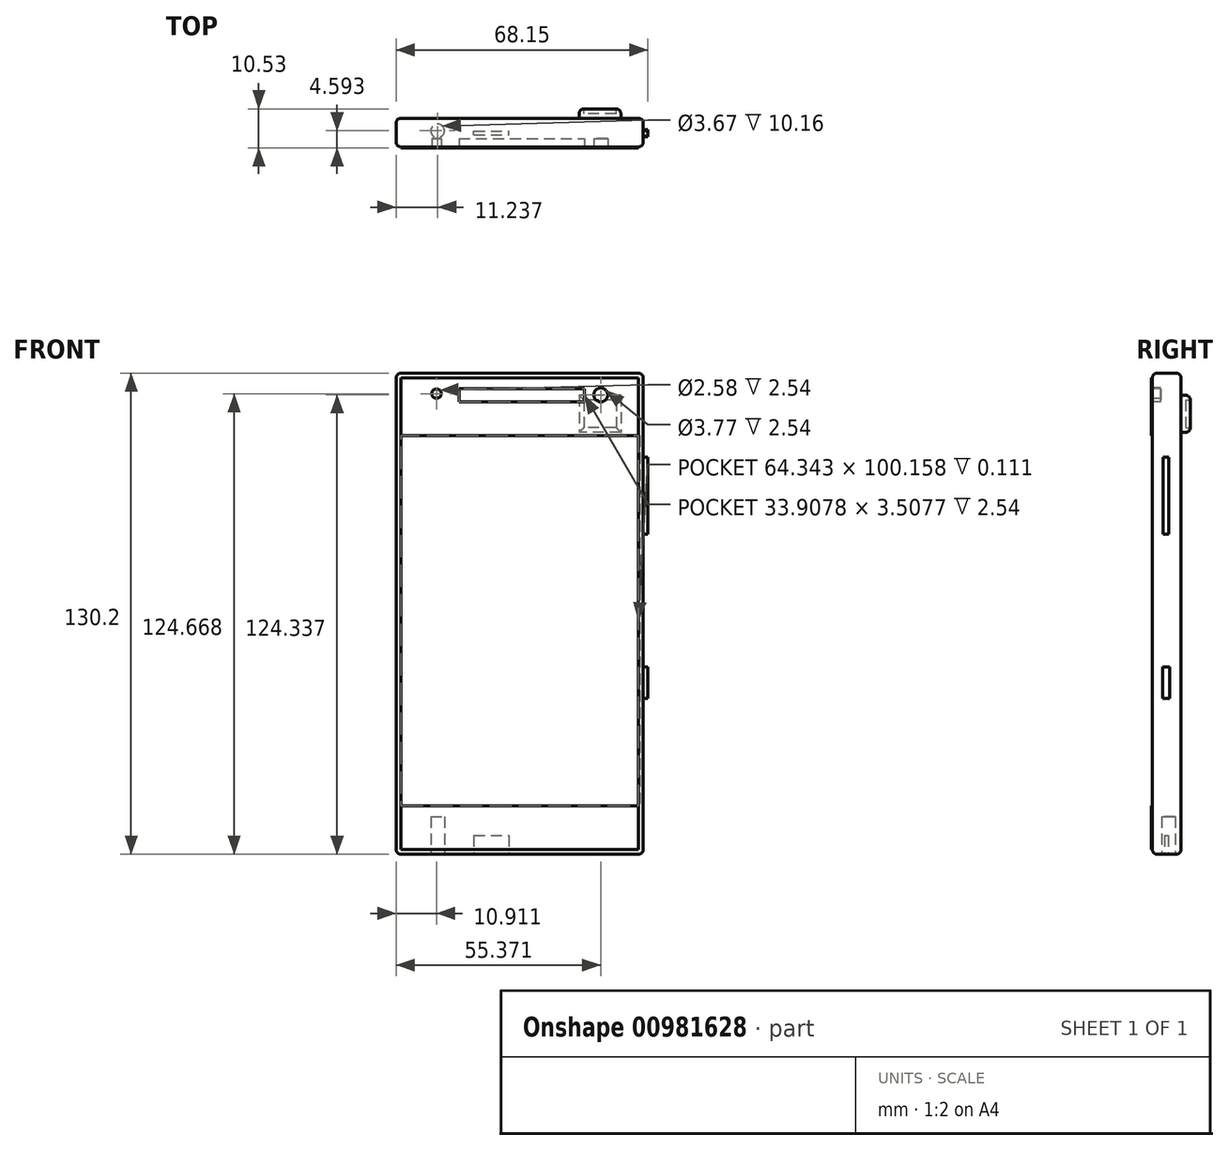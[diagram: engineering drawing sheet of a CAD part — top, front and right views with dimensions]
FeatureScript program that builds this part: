
annotation { "Feature Type Name" : "Feature", "Feature Type Description" : "" }
export const myFeature = defineFeature(function(context is Context, id is Id, definition is map)
    precondition{}
    {
        {
            var Q0;
            Q0=qCreatedBy(makeId("Front.planeOp"),FACE);
            var sketch = newSketch(context, id + "F0", { "sketchPlane" : qUnion([Q0])});
            skLineSegment(sketch, "E0.bottom", {"start": v(33.44, -65.1) * mm, "end": v(-33.44, -65.1) * mm});
            skLineSegment(sketch, "E0.top", {"start": v(33.44, 65.1) * mm, "end": v(-33.44, 65.1) * mm});
            skLineSegment(sketch, "E0.left", {"start": v(33.44, -65.1) * mm, "end": v(33.44, 65.1) * mm});
            skLineSegment(sketch, "E0.right", {"start": v(-33.44, -65.1) * mm, "end": v(-33.44, 65.1) * mm});
            skPoint(sketch, "E0.middle", {"position": v(0, 0) * mm});
            skSolve(sketch);
        }
        {
            var Q0;
            Q0 = qSketchRegion(id + "F0", true);
            extrude(context, id + "F1", {"entities" : qUnion([Q0]), "depth" : 7.73 * mm, "offsetDistance" : 25.4 * mm});
        }
        {
            var Q0;
            Q0=makeQuery(id+"F1.opExtrude","CAP_FACE",FACE,{"disambiguationData":[OSD([sQuery(id+"F0.wireOp",EDGE,"E0.bottom"),sQuery(id+"F0.wireOp",EDGE,"E0.top"),sQuery(id+"F0.wireOp",EDGE,"E0.left"),sQuery(id+"F0.wireOp",EDGE,"E0.right")])],"isStart":false});
            var Q1;
            Q1=makeQuery(id+"F1.opExtrude","CAP_FACE",FACE,{"disambiguationData":[OSD([sQuery(id+"F0.wireOp",EDGE,"E0.bottom"),sQuery(id+"F0.wireOp",EDGE,"E0.top"),sQuery(id+"F0.wireOp",EDGE,"E0.left"),sQuery(id+"F0.wireOp",EDGE,"E0.right")])],"isStart":true});
            var Q2;
            Q2=makeQuery(id+"F1.opExtrude","SWEPT_EDGE",EDGE,{"disambiguationData":[OSD([sQuery(id+"F0.wireOp",EDGE,"E0.top"),sQuery(id+"F0.wireOp",EDGE,"E0.right")])]});
            var Q3;
            Q3=makeQuery(id+"F1.opExtrude","SWEPT_EDGE",EDGE,{"disambiguationData":[OSD([sQuery(id+"F0.wireOp",EDGE,"E0.bottom"),sQuery(id+"F0.wireOp",EDGE,"E0.left")])]});
            var Q4;
            Q4=makeQuery(id+"F1.opExtrude","SWEPT_EDGE",EDGE,{"disambiguationData":[OSD([sQuery(id+"F0.wireOp",EDGE,"E0.top"),sQuery(id+"F0.wireOp",EDGE,"E0.left")])]});
            var Q5;
            Q5=makeQuery(id+"F1.opExtrude","SWEPT_EDGE",EDGE,{"disambiguationData":[OSD([sQuery(id+"F0.wireOp",EDGE,"E0.bottom"),sQuery(id+"F0.wireOp",EDGE,"E0.right")])]});
            fillet(context, id + "F2", {"entities" : qUnion([Q0, Q1, Q2, Q3, Q4, Q5]), "radius" : 1.27 * mm, "tangentPropagation" : true, "allowEdgeOverflow" : false});
        }
        {
            var Q0;
            Q0=qCreatedBy(makeId("Front.planeOp"),FACE);
            var sketch = newSketch(context, id + "F3", { "sketchPlane" : qUnion([Q0])});
            skLineSegment(sketch, "E1.bottom", {"start": v(-32.55, -50.39) * mm, "end": v(32.55, -50.39) * mm});
            skLineSegment(sketch, "E1.top", {"start": v(-32.55, 50.39) * mm, "end": v(32.55, 50.39) * mm});
            skLineSegment(sketch, "E1.left", {"start": v(-32.55, -50.39) * mm, "end": v(-32.55, 50.39) * mm});
            skLineSegment(sketch, "E1.right", {"start": v(32.55, -50.39) * mm, "end": v(32.55, 50.39) * mm});
            skSolve(sketch);
        }
        {
            var Q0;
            Q0 = qSketchRegion(id + "F3", true);
            var Q1;
            Q1=makeQuery(id+"F1.opExtrude","CAP_FACE",FACE,{"disambiguationData":[OSD([sQuery(id+"F0.wireOp",EDGE,"E0.bottom"),sQuery(id+"F0.wireOp",EDGE,"E0.top"),sQuery(id+"F0.wireOp",EDGE,"E0.left"),sQuery(id+"F0.wireOp",EDGE,"E0.right")])],"isStart":false});
            extrude(context, id + "F4", {"entities" : qUnion([Q0, Q1]), "operationType" : NewBodyOperationType.REMOVE, "oppositeDirection" : true, "depth" : 2.3 * mm, "offsetDistance" : 25.4 * mm});
        }
        {
            var Q0;
            Q0=qCreatedBy(makeId("Front.planeOp"),FACE);
            var sketch = newSketch(context, id + "F5", { "sketchPlane" : qUnion([Q0])});
            skLineSegment(sketch, "E2.bottom", {"start": v(-32.44, 48.2) * mm, "end": v(32.5, 48.2) * mm});
            skLineSegment(sketch, "E2.top", {"start": v(-32.44, -51.95) * mm, "end": v(32.5, -51.95) * mm});
            skLineSegment(sketch, "E2.left", {"start": v(-32.44, 48.2) * mm, "end": v(-32.44, -51.95) * mm});
            skLineSegment(sketch, "E2.right", {"start": v(32.5, 48.2) * mm, "end": v(32.5, -51.95) * mm});
            skSolve(sketch);
        }
        {
            var Q0;
            Q0 = qSketchRegion(id + "F5", true);
            extrude(context, id + "F6", {"entities" : qUnion([Q0]), "operationType" : NewBodyOperationType.ADD, "depth" : 7.62 * mm, "offsetDistance" : 25.4 * mm});
        }
        {
            var Q0;
            {var subQ0=sQuery(id+"F0.wireOp",EDGE,"E0.right");var subQ1=sQuery(id+"F0.wireOp",EDGE,"E0.left");var subQ2=sQuery(id+"F0.wireOp",EDGE,"E0.top");var subQ3=sQuery(id+"F0.wireOp",EDGE,"E0.bottom");Q0=makeQuery(id+"F6.boolean.opBoolean","SPLIT",FACE,{"disambiguationData":[TD([makeQuery(id+"F6.opExtrude","SWEPT_FACE",FACE,{"disambiguationData":[OSD([sQuery(id+"F5.wireOp",EDGE,"E2.bottom")])]})])],"derivedFrom":makeQuery(id+"F4.boolean.opBoolean","COPY",FACE,{"derivedFrom":makeQuery(id+"F4.opExtrude","CAP_FACE",FACE,{"disambiguationData":[OSD([subQ3,subQ2,subQ1,subQ0])],"isStart":false})})});}
            var sketch = newSketch(context, id + "F7", { "sketchPlane" : qUnion([Q0])});
            skLineSegment(sketch, "E3.bottom", {"start": v(-32.17, 48.2) * mm, "end": v(32.17, 48.2) * mm});
            skLineSegment(sketch, "E3.top", {"start": v(-32.17, 63.83) * mm, "end": v(32.17, 63.83) * mm});
            skLineSegment(sketch, "E3.left", {"start": v(-32.17, 48.2) * mm, "end": v(-32.17, 63.83) * mm});
            skLineSegment(sketch, "E3.right", {"start": v(32.17, 48.2) * mm, "end": v(32.17, 63.83) * mm});
            skSolve(sketch);
        }
        {
            var Q0;
            Q0 = qSketchRegion(id + "F7", true);
            extrude(context, id + "F8", {"entities" : qUnion([Q0]), "operationType" : NewBodyOperationType.ADD, "depth" : 2.54 * mm, "offsetDistance" : 25.4 * mm});
        }
        {
            var Q0;
            Q0=makeQuery(id+"F8.opExtrude","CAP_FACE",FACE,{"disambiguationData":[OSD([sQuery(id+"F7.wireOp",EDGE,"E3.bottom"),sQuery(id+"F7.wireOp",EDGE,"E3.top"),sQuery(id+"F7.wireOp",EDGE,"E3.left"),sQuery(id+"F7.wireOp",EDGE,"E3.right")])],"isStart":false});
            var sketch = newSketch(context, id + "F9", { "sketchPlane" : qUnion([Q0])});
            skLineSegment(sketch, "E4.bottom", {"start": v(-16.45, 60.86) * mm, "end": v(17.46, 60.86) * mm});
            skLineSegment(sketch, "E4.top", {"start": v(-16.45, 57.35) * mm, "end": v(17.46, 57.35) * mm});
            skLineSegment(sketch, "E4.left", {"start": v(-16.45, 60.86) * mm, "end": v(-16.45, 57.35) * mm});
            skLineSegment(sketch, "E4.right", {"start": v(17.46, 60.86) * mm, "end": v(17.46, 57.35) * mm});
            skCircle(sketch, "E5", {"center": v(-22.53, 59.57) * mm, "radius": 1.29 * mm});
            skCircle(sketch, "E6", {"center": v(21.93, 59.24) * mm, "radius": 1.89 * mm});
            skSolve(sketch);
        }
        {
            var Q0;
            Q0 = qSketchRegion(id + "F9", true);
            extrude(context, id + "F10", {"entities" : qUnion([Q0]), "operationType" : NewBodyOperationType.REMOVE, "oppositeDirection" : true, "depth" : 2.54 * mm, "offsetDistance" : 25.4 * mm});
        }
        {
            var Q0;
            Q0 = qSketchRegion(id + "F9", true);
            extrude(context, id + "F11", {"entities" : qUnion([Q0]), "operationType" : NewBodyOperationType.REMOVE, "oppositeDirection" : true, "depth" : 2.54 * mm, "offsetDistance" : 25.4 * mm});
        }
        {
            var Q0;
            {var subQ0=sQuery(id+"F0.wireOp",EDGE,"E0.right");var subQ1=sQuery(id+"F0.wireOp",EDGE,"E0.left");var subQ2=sQuery(id+"F0.wireOp",EDGE,"E0.top");var subQ3=sQuery(id+"F0.wireOp",EDGE,"E0.bottom");Q0=makeQuery(id+"F6.boolean.opBoolean","SPLIT",FACE,{"disambiguationData":[TD([makeQuery(id+"F6.opExtrude","SWEPT_FACE",FACE,{"disambiguationData":[OSD([sQuery(id+"F5.wireOp",EDGE,"E2.top")])]})])],"derivedFrom":makeQuery(id+"F4.boolean.opBoolean","COPY",FACE,{"derivedFrom":makeQuery(id+"F4.opExtrude","CAP_FACE",FACE,{"disambiguationData":[OSD([subQ3,subQ2,subQ1,subQ0])],"isStart":false})})});}
            var sketch = newSketch(context, id + "F12", { "sketchPlane" : qUnion([Q0])});
            skLineSegment(sketch, "E7.bottom", {"start": v(-32.17, -63.83) * mm, "end": v(32.17, -63.83) * mm});
            skLineSegment(sketch, "E7.top", {"start": v(-32.17, -51.95) * mm, "end": v(32.17, -51.95) * mm});
            skLineSegment(sketch, "E7.left", {"start": v(-32.17, -63.83) * mm, "end": v(-32.17, -51.95) * mm});
            skLineSegment(sketch, "E7.right", {"start": v(32.17, -63.83) * mm, "end": v(32.17, -51.95) * mm});
            skSolve(sketch);
        }
        {
            var Q0;
            Q0 = qSketchRegion(id + "F12", true);
            extrude(context, id + "F13", {"entities" : qUnion([Q0]), "operationType" : NewBodyOperationType.ADD, "depth" : 2.54 * mm, "offsetDistance" : 25.4 * mm});
        }
        {
            var Q0;
            Q0=makeQuery(id+"F0.imprint","IMPRINT",FACE,{"disambiguationData":[TD([[makeQuery(id+"F0.imprint","IMPRINT",EDGE,{"derivedFrom":sQuery(id+"F0.wireOp",EDGE,"E0.bottom")}),-1.0]])]});
            var sketch = newSketch(context, id + "F14", { "sketchPlane" : qUnion([Q0])});
            skLineSegment(sketch, "E8.bottom", {"start": v(27.36, 59.12) * mm, "end": v(16.08, 59.12) * mm});
            skLineSegment(sketch, "E8.top", {"start": v(27.36, 49.08) * mm, "end": v(16.08, 49.08) * mm});
            skLineSegment(sketch, "E8.left", {"start": v(27.36, 59.12) * mm, "end": v(27.36, 49.08) * mm});
            skLineSegment(sketch, "E8.right", {"start": v(16.08, 59.12) * mm, "end": v(16.08, 49.08) * mm});
            skSolve(sketch);
        }
        {
            var Q0;
            Q0 = qSketchRegion(id + "F14", true);
            extrude(context, id + "F15", {"entities" : qUnion([Q0]), "operationType" : NewBodyOperationType.ADD, "oppositeDirection" : true, "depth" : 2.54 * mm, "offsetDistance" : 25.4 * mm});
        }
        {
            var Q0;
            Q0=makeQuery(id+"F15.opExtrude","CAP_FACE",FACE,{"disambiguationData":[OSD([sQuery(id+"F14.wireOp",EDGE,"E8.bottom"),sQuery(id+"F14.wireOp",EDGE,"E8.top"),sQuery(id+"F14.wireOp",EDGE,"E8.left"),sQuery(id+"F14.wireOp",EDGE,"E8.right")])],"isStart":false});
            fillet(context, id + "F16", {"entities" : qUnion([Q0]), "radius" : 1.27 * mm, "tangentPropagation" : true, "allowEdgeOverflow" : false});
        }
        {
            var Q0;
            Q0=makeQuery(id+"F15.opExtrude","CAP_FACE",FACE,{"disambiguationData":[OSD([sQuery(id+"F14.wireOp",EDGE,"E8.bottom"),sQuery(id+"F14.wireOp",EDGE,"E8.top"),sQuery(id+"F14.wireOp",EDGE,"E8.left"),sQuery(id+"F14.wireOp",EDGE,"E8.right")])],"isStart":false});
            var sketch = newSketch(context, id + "F17", { "sketchPlane" : qUnion([Q0])});
            skLineSegment(sketch, "E9.bottom", {"start": v(-26.1, 50.35) * mm, "end": v(-17.35, 50.35) * mm});
            skLineSegment(sketch, "E9.top", {"start": v(-26.1, 57.85) * mm, "end": v(-17.35, 57.85) * mm});
            skLineSegment(sketch, "E9.left", {"start": v(-26.1, 50.35) * mm, "end": v(-26.1, 57.85) * mm});
            skLineSegment(sketch, "E9.right", {"start": v(-17.35, 50.35) * mm, "end": v(-17.35, 57.85) * mm});
            skSolve(sketch);
        }
        {
            var Q0;
            Q0 = qSketchRegion(id + "F17", true);
            extrude(context, id + "F18", {"entities" : qUnion([Q0]), "operationType" : NewBodyOperationType.REMOVE, "oppositeDirection" : true, "depth" : 1.27 * mm, "offsetDistance" : 25.4 * mm});
        }
        {
            var Q0;
            Q0=makeQuery(id+"F1.opExtrude","SWEPT_FACE",FACE,{"disambiguationData":[OSD([sQuery(id+"F0.wireOp",EDGE,"E0.bottom")])]});
            var sketch = newSketch(context, id + "F19", { "sketchPlane" : qUnion([Q0])});
            skCircle(sketch, "E10", {"center": v(-22.2, 3.4) * mm, "radius": 1.83 * mm});
            skSolve(sketch);
        }
        {
            var Q0;
            Q0 = qSketchRegion(id + "F19", true);
            extrude(context, id + "F20", {"entities" : qUnion([Q0]), "operationType" : NewBodyOperationType.REMOVE, "oppositeDirection" : true, "depth" : 10.16 * mm, "offsetDistance" : 25.4 * mm});
        }
        {
            var Q0;
            Q0=makeQuery(id+"F1.opExtrude","SWEPT_FACE",FACE,{"disambiguationData":[OSD([sQuery(id+"F0.wireOp",EDGE,"E0.bottom")])]});
            var sketch = newSketch(context, id + "F21", { "sketchPlane" : qUnion([Q0])});
            skLineSegment(sketch, "E11.bottom", {"start": v(-12.41, 4.47) * mm, "end": v(-2.9, 4.47) * mm});
            skLineSegment(sketch, "E11.top", {"start": v(-12.41, 3.41) * mm, "end": v(-2.9, 3.41) * mm});
            skLineSegment(sketch, "E11.left", {"start": v(-12.41, 4.47) * mm, "end": v(-12.41, 3.41) * mm});
            skLineSegment(sketch, "E11.right", {"start": v(-2.9, 4.47) * mm, "end": v(-2.9, 3.41) * mm});
            skSolve(sketch);
        }
        {
            var Q0;
            Q0 = qSketchRegion(id + "F21", true);
            extrude(context, id + "F22", {"entities" : qUnion([Q0]), "operationType" : NewBodyOperationType.REMOVE, "oppositeDirection" : true, "depth" : 5.08 * mm, "offsetDistance" : 25.4 * mm});
        }
        {
            var Q0;
            Q0=makeQuery(id+"F1.opExtrude","SWEPT_FACE",FACE,{"disambiguationData":[OSD([sQuery(id+"F0.wireOp",EDGE,"E0.left")])]});
            var sketch = newSketch(context, id + "F23", { "sketchPlane" : qUnion([Q0])});
            skLineSegment(sketch, "E12.bottom", {"start": v(-4.9, 42.33) * mm, "end": v(-3.29, 42.33) * mm});
            skLineSegment(sketch, "E12.top", {"start": v(-4.9, 21.48) * mm, "end": v(-3.29, 21.48) * mm});
            skLineSegment(sketch, "E12.left", {"start": v(-4.9, 42.33) * mm, "end": v(-4.9, 21.48) * mm});
            skLineSegment(sketch, "E12.right", {"start": v(-3.29, 42.33) * mm, "end": v(-3.29, 21.48) * mm});
            skLineSegment(sketch, "E13.bottom", {"start": v(-4.93, -14.36) * mm, "end": v(-3.06, -14.36) * mm});
            skLineSegment(sketch, "E13.top", {"start": v(-4.93, -22.95) * mm, "end": v(-3.06, -22.95) * mm});
            skLineSegment(sketch, "E13.left", {"start": v(-4.93, -14.36) * mm, "end": v(-4.93, -22.95) * mm});
            skLineSegment(sketch, "E13.right", {"start": v(-3.06, -14.36) * mm, "end": v(-3.06, -22.95) * mm});
            skSolve(sketch);
        }
        {
            var Q0;
            Q0 = qSketchRegion(id + "F23", true);
            extrude(context, id + "F24", {"entities" : qUnion([Q0]), "operationType" : NewBodyOperationType.ADD, "depth" : 1.27 * mm, "offsetDistance" : 25.4 * mm});
        }
    });
